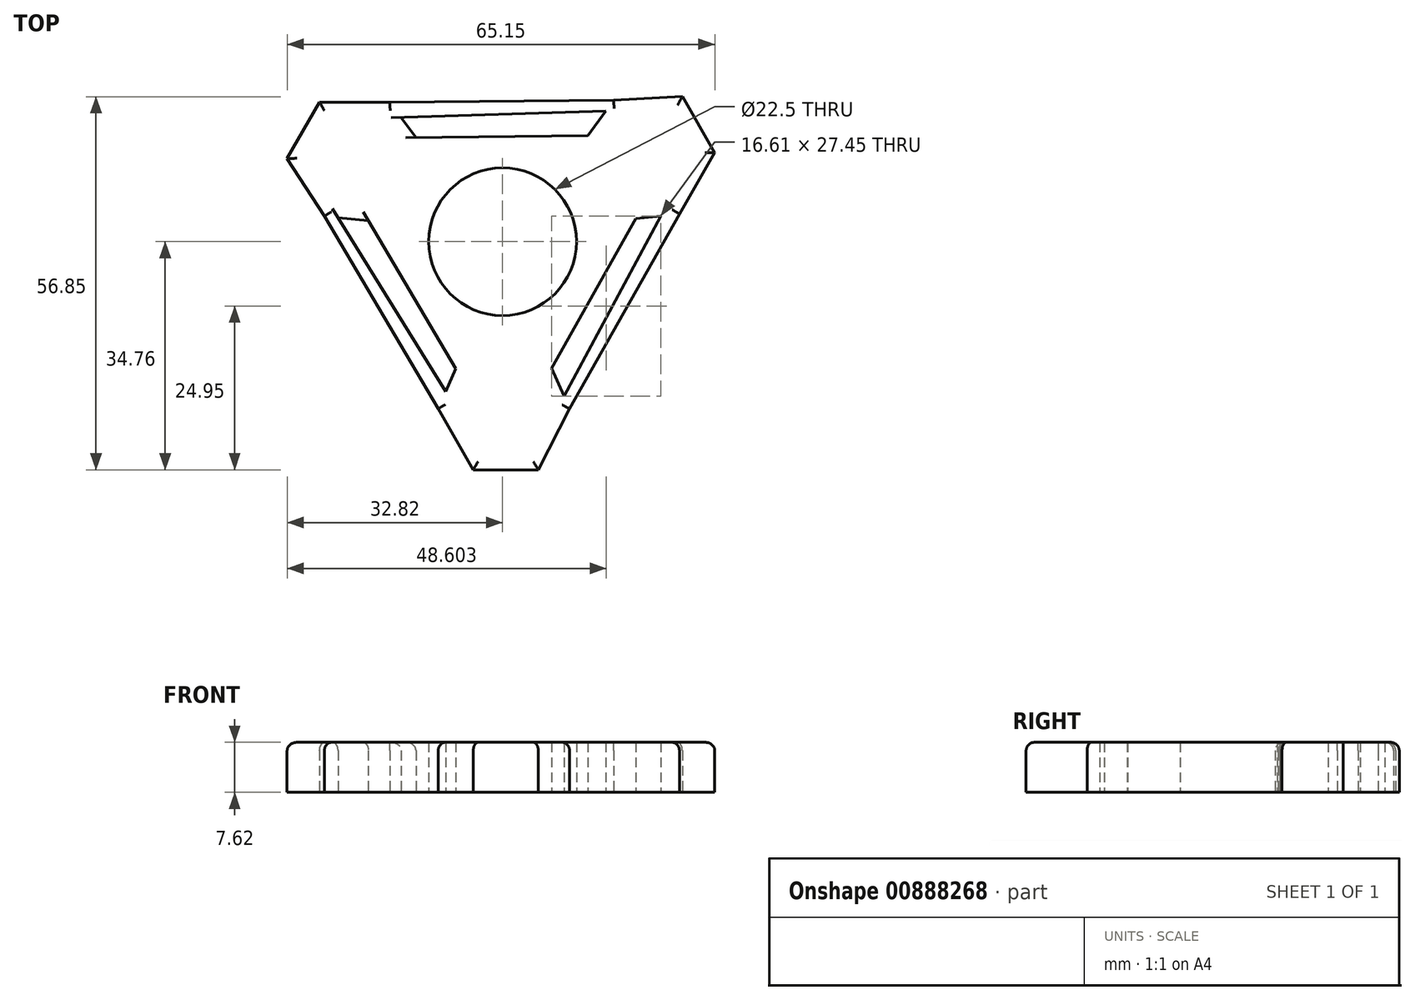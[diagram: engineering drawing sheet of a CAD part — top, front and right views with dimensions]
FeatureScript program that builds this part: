
annotation { "Feature Type Name" : "Feature", "Feature Type Description" : "" }
export const myFeature = defineFeature(function(context is Context, id is Id, definition is map)
    precondition{}
    {
        {
            var Q0;
            Q0=qCreatedBy(makeId("Top.planeOp"),FACE);
            var sketch = newSketch(context, id + "F0", { "sketchPlane" : qUnion([Q0])});
            skCircle(sketch, "E0", {"center": v(0, 0) * mm, "radius": 11.25 * mm});
            skCircle(sketch, "E1", {"center": v(0, 0) * mm, "radius": 13.97 * mm});
            skLineSegment(sketch, "E2", {"start": v(4.76, -13.14) * mm, "end": v(10.2, -25.45) * mm});
            skLineSegment(sketch, "E3", {"start": v(10.2, -25.45) * mm, "end": v(5.45, -34.76) * mm});
            skLineSegment(sketch, "E4", {"start": v(5.45, -34.76) * mm, "end": v(-4.46, -34.76) * mm});
            skLineSegment(sketch, "E5", {"start": v(-4.46, -34.76) * mm, "end": v(-9.8, -25.45) * mm});
            skLineSegment(sketch, "E6", {"start": v(-9.8, -25.45) * mm, "end": v(-4.46, -13.24) * mm});
            skLineSegment(sketch, "E7.1.0", {"start": v(32.33, 13.52) * mm, "end": v(26.94, 4.23) * mm});
            skLineSegment(sketch, "E7.1.1", {"start": v(9, 10.69) * mm, "end": v(16.94, 21.56) * mm});
            skLineSegment(sketch, "E7.1.2", {"start": v(26.94, 4.23) * mm, "end": v(13.7, 2.76) * mm});
            skLineSegment(sketch, "E7.1.3", {"start": v(16.94, 21.56) * mm, "end": v(27.38, 22.1) * mm});
            skLineSegment(sketch, "E7.1.4", {"start": v(27.38, 22.1) * mm, "end": v(32.33, 13.52) * mm});
            skLineSegment(sketch, "E7.2.0", {"start": v(-27.87, 21.24) * mm, "end": v(-17.14, 21.21) * mm});
            skLineSegment(sketch, "E7.2.1", {"start": v(-13.75, 2.45) * mm, "end": v(-27.14, 3.9) * mm});
            skLineSegment(sketch, "E7.2.2", {"start": v(-17.14, 21.21) * mm, "end": v(-9.24, 10.48) * mm});
            skLineSegment(sketch, "E7.2.3", {"start": v(-27.14, 3.9) * mm, "end": v(-32.82, 12.66) * mm});
            skLineSegment(sketch, "E7.2.4", {"start": v(-32.82, 12.66) * mm, "end": v(-27.87, 21.24) * mm});
            skLineSegment(sketch, "E8", {"start": v(7.48, -19.3) * mm, "end": v(20.32, 3.5) * mm});
            skLineSegment(sketch, "E9.1.0", {"start": v(12.97, 16.12) * mm, "end": v(-13.19, 15.85) * mm});
            skLineSegment(sketch, "E9.2.0", {"start": v(-20.45, 3.17) * mm, "end": v(-7.13, -19.34) * mm});
            skLineSegment(sketch, "E10", {"start": v(24.09, 3.92) * mm, "end": v(9.35, -23.54) * mm});
            skLineSegment(sketch, "E11", {"start": v(26.94, 4.23) * mm, "end": v(10.2, -25.45) * mm});
            skLineSegment(sketch, "E12.1.0", {"start": v(-15.44, 18.9) * mm, "end": v(15.7, 19.87) * mm});
            skLineSegment(sketch, "E12.1.1", {"start": v(-17.14, 21.21) * mm, "end": v(16.94, 21.56) * mm});
            skLineSegment(sketch, "E12.2.0", {"start": v(-8.65, -22.82) * mm, "end": v(-25.06, 3.67) * mm});
            skLineSegment(sketch, "E12.2.1", {"start": v(-9.8, -25.45) * mm, "end": v(-27.14, 3.9) * mm});
            skSolve(sketch);
        }
        {
            var Q0;
            {var subQ5=sQuery(id+"F0.wireOp",EDGE,"E7.2.0");Q0=makeQuery(id+"F0.imprint","IMPRINT",FACE,{"disambiguationData":[TD([[makeQuery(id+"F0.imprint","IMPRINT",EDGE,{"derivedFrom":subQ5}),-1.0]])]});}
            var Q1;
            {var subQ5=sQuery(id+"F0.wireOp",EDGE,"E7.1.0");Q1=makeQuery(id+"F0.imprint","IMPRINT",FACE,{"disambiguationData":[TD([[makeQuery(id+"F0.imprint","IMPRINT",EDGE,{"derivedFrom":subQ5}),-1.0]])]});}
            var Q2;
            {var subQ0=sQuery(id+"F0.wireOp",EDGE,"E3");Q2=makeQuery(id+"F0.imprint","IMPRINT",FACE,{"disambiguationData":[TD([[makeQuery(id+"F0.imprint","IMPRINT",EDGE,{"derivedFrom":subQ0}),-1.0]])]});}
            var Q3;
            {var subQ2=sQuery(id+"F0.wireOp",EDGE,"E10");Q3=makeQuery(id+"F0.imprint","IMPRINT",FACE,{"disambiguationData":[TD([[makeQuery(id+"F0.imprint","IMPRINT",EDGE,{"derivedFrom":subQ2}),1.0]])]});}
            var Q4;
            {var subQ5=sQuery(id+"F0.wireOp",EDGE,"E8");Q4=makeQuery(id+"F0.imprint","IMPRINT",FACE,{"disambiguationData":[TD([[makeQuery(id+"F0.imprint","IMPRINT",EDGE,{"derivedFrom":subQ5}),1.0]])]});}
            var Q5;
            {var subQ5=sQuery(id+"F0.wireOp",EDGE,"E9.2.0");Q5=makeQuery(id+"F0.imprint","IMPRINT",FACE,{"disambiguationData":[TD([[makeQuery(id+"F0.imprint","IMPRINT",EDGE,{"derivedFrom":subQ5}),1.0]])]});}
            var Q6;
            {var subQ5=sQuery(id+"F0.wireOp",EDGE,"E9.1.0");Q6=makeQuery(id+"F0.imprint","IMPRINT",FACE,{"disambiguationData":[TD([[makeQuery(id+"F0.imprint","IMPRINT",EDGE,{"derivedFrom":subQ5}),1.0]])]});}
            var Q7;
            {var subQ2=sQuery(id+"F0.wireOp",EDGE,"E12.1.0");Q7=makeQuery(id+"F0.imprint","IMPRINT",FACE,{"disambiguationData":[TD([[makeQuery(id+"F0.imprint","IMPRINT",EDGE,{"derivedFrom":subQ2}),1.0]])]});}
            var Q8;
            {var subQ2=sQuery(id+"F0.wireOp",EDGE,"E12.2.0");Q8=makeQuery(id+"F0.imprint","IMPRINT",FACE,{"disambiguationData":[TD([[makeQuery(id+"F0.imprint","IMPRINT",EDGE,{"derivedFrom":subQ2}),1.0]])]});}
            var Q9;
            Q9=makeQuery(id+"F0.imprint","IMPRINT",FACE,{"disambiguationData":[TD([[makeQuery(id+"F0.imprint","IMPRINT",EDGE,{"derivedFrom":sQuery(id+"F0.wireOp",EDGE,"E0")}),-1.0]])]});
            extrude(context, id + "F1", {"entities" : qUnion([Q0, Q1, Q2, Q3, Q4, Q5, Q6, Q7, Q8, Q9]), "depth" : 7.62 * mm, "offsetDistance" : 25.4 * mm});
        }
        {
            var Q0;
            Q0=makeQuery(id+"F1.opExtrude","CAP_EDGE",EDGE,{"disambiguationData":[OSD([sQuery(id+"F0.wireOp",EDGE,"E7.2.1")])],"isStart":false});
            var Q1;
            Q1=makeQuery(id+"F1.opExtrude","CAP_EDGE",EDGE,{"disambiguationData":[OSD([sQuery(id+"F0.wireOp",EDGE,"E7.2.2")])],"isStart":false});
            var Q2;
            Q2=makeQuery(id+"F1.opExtrude","CAP_EDGE",EDGE,{"disambiguationData":[OSD([sQuery(id+"F0.wireOp",EDGE,"E7.2.0")])],"isStart":false});
            var Q3;
            Q3=makeQuery(id+"F1.opExtrude","CAP_EDGE",EDGE,{"disambiguationData":[OSD([sQuery(id+"F0.wireOp",EDGE,"E7.2.4")])],"isStart":false});
            var Q4;
            Q4=makeQuery(id+"F1.opExtrude","CAP_EDGE",EDGE,{"disambiguationData":[OSD([sQuery(id+"F0.wireOp",EDGE,"E7.2.3")])],"isStart":false});
            var Q5;
            Q5=makeQuery(id+"F1.opExtrude","CAP_EDGE",EDGE,{"disambiguationData":[OSD([sQuery(id+"F0.wireOp",EDGE,"E12.1.1")])],"isStart":false});
            var Q6;
            Q6=makeQuery(id+"F1.opExtrude","CAP_EDGE",EDGE,{"disambiguationData":[OSD([sQuery(id+"F0.wireOp",EDGE,"E7.1.3")])],"isStart":false});
            var Q7;
            Q7=makeQuery(id+"F1.opExtrude","CAP_EDGE",EDGE,{"disambiguationData":[OSD([sQuery(id+"F0.wireOp",EDGE,"E7.1.4")])],"isStart":false});
            var Q8;
            Q8=makeQuery(id+"F1.opExtrude","CAP_EDGE",EDGE,{"disambiguationData":[OSD([sQuery(id+"F0.wireOp",EDGE,"E7.1.0")])],"isStart":false});
            var Q9;
            Q9=makeQuery(id+"F1.opExtrude","CAP_EDGE",EDGE,{"disambiguationData":[OSD([sQuery(id+"F0.wireOp",EDGE,"E11")])],"isStart":false});
            var Q10;
            Q10=makeQuery(id+"F1.opExtrude","CAP_EDGE",EDGE,{"disambiguationData":[OSD([sQuery(id+"F0.wireOp",EDGE,"E3")])],"isStart":false});
            var Q11;
            Q11=makeQuery(id+"F1.opExtrude","CAP_EDGE",EDGE,{"disambiguationData":[OSD([sQuery(id+"F0.wireOp",EDGE,"E4")])],"isStart":false});
            var Q12;
            Q12=makeQuery(id+"F1.opExtrude","CAP_EDGE",EDGE,{"disambiguationData":[OSD([sQuery(id+"F0.wireOp",EDGE,"E5")])],"isStart":false});
            var Q13;
            Q13=makeQuery(id+"F1.opExtrude","CAP_EDGE",EDGE,{"disambiguationData":[OSD([sQuery(id+"F0.wireOp",EDGE,"E12.2.1")])],"isStart":false});
            fillet(context, id + "F2", {"entities" : qUnion([Q0, Q1, Q2, Q3, Q4, Q5, Q6, Q7, Q8, Q9, Q10, Q11, Q12, Q13]), "radius" : 1.27 * mm, "tangentPropagation" : true, "allowEdgeOverflow" : false});
        }
    });
